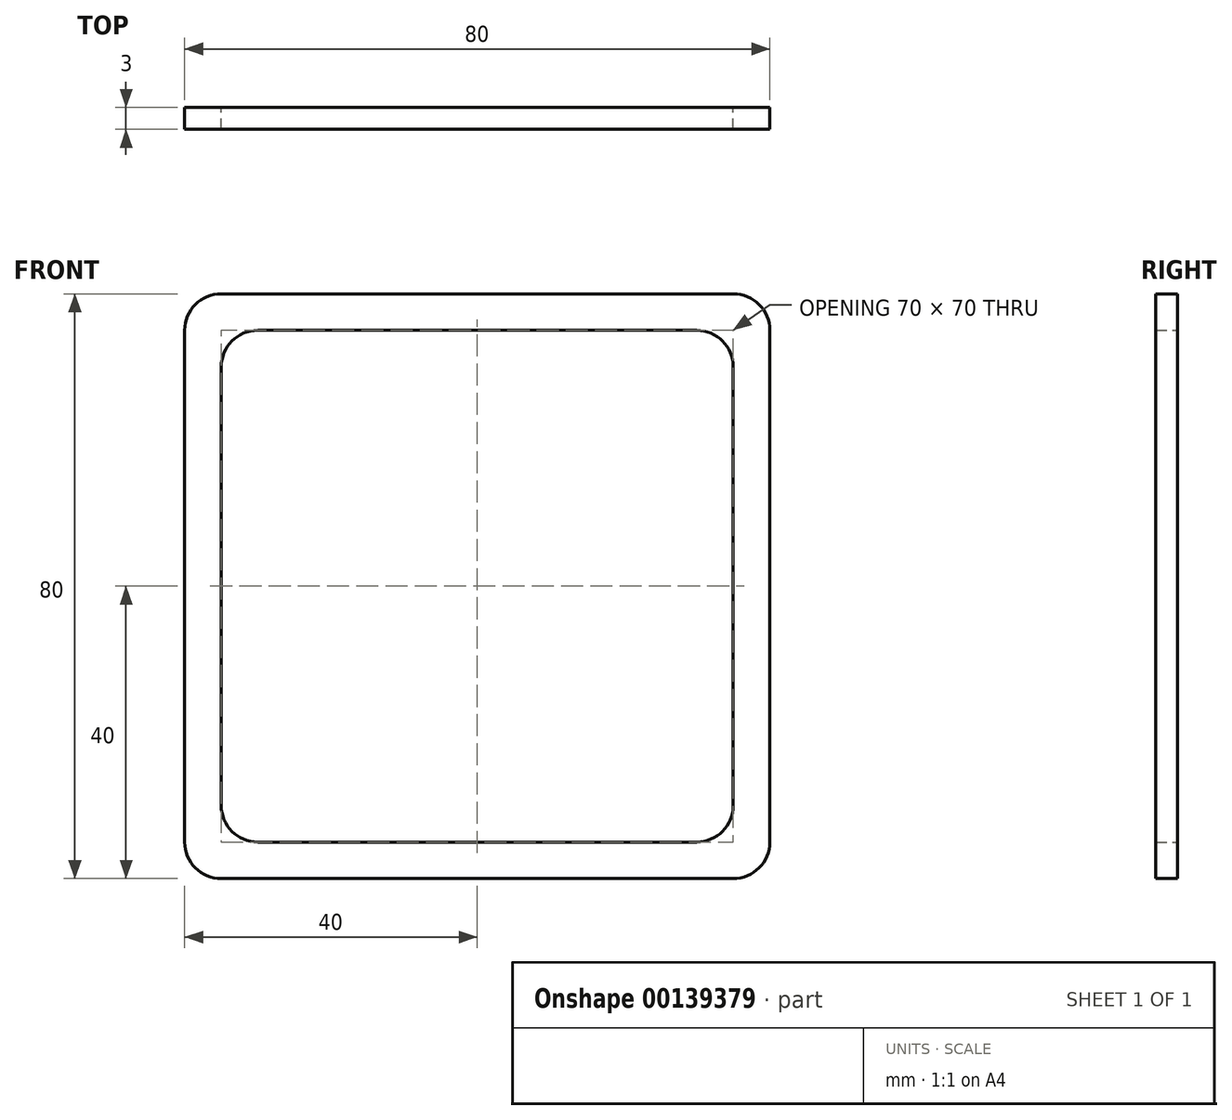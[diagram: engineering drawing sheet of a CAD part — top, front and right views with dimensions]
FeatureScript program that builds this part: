
annotation { "Feature Type Name" : "Feature", "Feature Type Description" : "" }
export const myFeature = defineFeature(function(context is Context, id is Id, definition is map)
    precondition{}
    {
        {
            var Q0;
            Q0=qCreatedBy(makeId("Front.planeOp"),FACE);
            var sketch = newSketch(context, id + "F0", { "sketchPlane" : qUnion([Q0])});
            skLineSegment(sketch, "E0.bottom", {"start": v(-5, 0) * mm, "end": v(-75, 0) * mm});
            skLineSegment(sketch, "E0.top", {"start": v(-5, 80) * mm, "end": v(-75, 80) * mm});
            skLineSegment(sketch, "E0.left", {"start": v(0, 5) * mm, "end": v(0, 75) * mm});
            skLineSegment(sketch, "E0.right", {"start": v(-80, 5) * mm, "end": v(-80, 75) * mm});
            skPoint(sketch, "E1.visualSharp", {"position": v(-80, 80) * mm});
            skArc(sketch, "E1.filletArc", {"start": v(-75, 80) * mm, "mid": v(-78.54, 78.54) * mm, "end": v(-80, 75) * mm});
            skPoint(sketch, "E2.visualSharp", {"position": v(0, 80) * mm});
            skArc(sketch, "E2.filletArc", {"start": v(0, 75) * mm, "mid": v(-1.46, 78.54) * mm, "end": v(-5, 80) * mm});
            skPoint(sketch, "E3.visualSharp", {"position": v(-80, 0) * mm});
            skArc(sketch, "E3.filletArc", {"start": v(-80, 5) * mm, "mid": v(-78.54, 1.46) * mm, "end": v(-75, 0) * mm});
            skPoint(sketch, "E4.visualSharp", {"position": v(0, 0) * mm});
            skArc(sketch, "E4.filletArc", {"start": v(-5, 0) * mm, "mid": v(-1.46, 1.46) * mm, "end": v(0, 5) * mm});
            skLineSegment(sketch, "E5.bottom", {"start": v(-70, 75) * mm, "end": v(-10, 75) * mm});
            skLineSegment(sketch, "E5.top", {"start": v(-70, 5) * mm, "end": v(-10, 5) * mm});
            skLineSegment(sketch, "E5.left", {"start": v(-75, 70) * mm, "end": v(-75, 10) * mm});
            skLineSegment(sketch, "E5.right", {"start": v(-5, 70) * mm, "end": v(-5, 10) * mm});
            skArc(sketch, "E6.filletArc", {"start": v(-70, 75) * mm, "mid": v(-73.54, 73.54) * mm, "end": v(-75, 70) * mm});
            skArc(sketch, "E7.filletArc", {"start": v(-5, 70) * mm, "mid": v(-6.46, 73.54) * mm, "end": v(-10, 75) * mm});
            skArc(sketch, "E8.filletArc", {"start": v(-10, 5) * mm, "mid": v(-6.46, 6.46) * mm, "end": v(-5, 10) * mm});
            skArc(sketch, "E9.filletArc", {"start": v(-75, 10) * mm, "mid": v(-73.54, 6.46) * mm, "end": v(-70, 5) * mm});
            skSolve(sketch);
        }
        {
            var Q0;
            Q0=makeQuery(id+"F0.imprint","IMPRINT",FACE,{"disambiguationData":[TD([[makeQuery(id+"F0.imprint","IMPRINT",EDGE,{"derivedFrom":sQuery(id+"F0.wireOp",EDGE,"E0.bottom")}),-1.0]])]});
            extrude(context, id + "F1", {"entities" : qUnion([Q0]), "depth" : 3 * mm});
        }
    });
